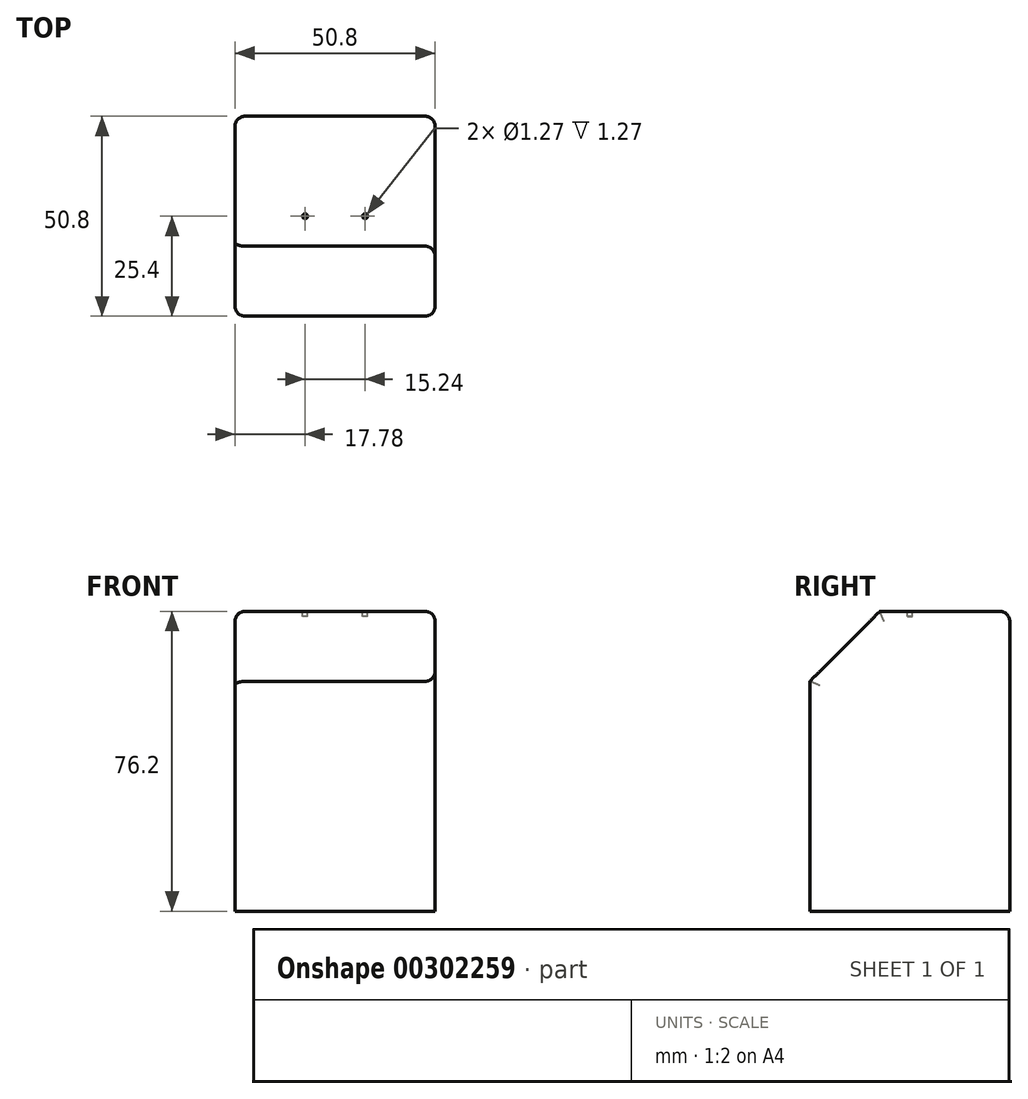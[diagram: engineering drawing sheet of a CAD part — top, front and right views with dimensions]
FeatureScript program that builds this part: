
annotation { "Feature Type Name" : "Feature", "Feature Type Description" : "" }
export const myFeature = defineFeature(function(context is Context, id is Id, definition is map)
    precondition{}
    {
        {
            var Q0;
            Q0=qCreatedBy(makeId("Top.planeOp"),FACE);
            var sketch = newSketch(context, id + "F0", { "sketchPlane" : qUnion([Q0])});
            skLineSegment(sketch, "E0.bottom", {"start": v(25.4, 25.4) * mm, "end": v(-25.4, 25.4) * mm});
            skLineSegment(sketch, "E0.top", {"start": v(25.4, -25.4) * mm, "end": v(-25.4, -25.4) * mm});
            skLineSegment(sketch, "E0.left", {"start": v(25.4, 25.4) * mm, "end": v(25.4, -25.4) * mm});
            skLineSegment(sketch, "E0.right", {"start": v(-25.4, 25.4) * mm, "end": v(-25.4, -25.4) * mm});
            skPoint(sketch, "E0.middle", {"position": v(0, 0) * mm});
            skSolve(sketch);
        }
        {
            var Q0;
            Q0 = qSketchRegion(id + "F0", true);
            extrude(context, id + "F1", {"entities" : qUnion([Q0]), "endBound" : BoundingType.SYMMETRIC, "depth" : 76.2 * mm});
        }
        {
            var Q0;
            Q0=makeQuery(id+"F1.opExtrude","CAP_FACE",FACE,{"disambiguationData":[OSD([sQuery(id+"F0.wireOp",EDGE,"E0.bottom"),sQuery(id+"F0.wireOp",EDGE,"E0.top"),sQuery(id+"F0.wireOp",EDGE,"E0.left"),sQuery(id+"F0.wireOp",EDGE,"E0.right")])],"isStart":false});
            var sketch = newSketch(context, id + "F2", { "sketchPlane" : qUnion([Q0])});
            skCircle(sketch, "E1", {"center": v(-7.62, 0) * mm, "radius": 0.64 * mm});
            skCircle(sketch, "E2", {"center": v(7.62, 0) * mm, "radius": 0.64 * mm});
            skSolve(sketch);
        }
        {
            var Q0;
            Q0 = qSketchRegion(id + "F2", true);
            extrude(context, id + "F3", {"entities" : qUnion([Q0]), "operationType" : NewBodyOperationType.REMOVE, "oppositeDirection" : true, "depth" : 1.27 * mm});
        }
        {
            var Q0;
            Q0=makeQuery(id+"F1.opExtrude","SWEPT_FACE",FACE,{"disambiguationData":[OSD([sQuery(id+"F0.wireOp",EDGE,"E0.left")])]});
            var sketch = newSketch(context, id + "F4", { "sketchPlane" : qUnion([Q0])});
            skLineSegment(sketch, "E3", {"start": v(-25.4, 20.32) * mm, "end": v(-7.62, 38.1) * mm});
            skLineSegment(sketch, "E4", {"start": v(-7.62, 38.1) * mm, "end": v(-25.4, 38.1) * mm});
            skLineSegment(sketch, "E5", {"start": v(-25.4, 38.1) * mm, "end": v(-25.4, 20.32) * mm});
            skSolve(sketch);
        }
        {
            var Q0;
            Q0 = qSketchRegion(id + "F4", true);
            extrude(context, id + "F5", {"entities" : qUnion([Q0]), "operationType" : NewBodyOperationType.REMOVE, "endBound" : BoundingType.THROUGH_ALL, "oppositeDirection" : true, "depth" : 25.4 * mm});
        }
        {
            var Q0;
            Q0=makeQuery(id+"F5.boolean.opBoolean","COPY",EDGE,{"derivedFrom":makeQuery(id+"F5.opExtrude","SWEPT_EDGE",EDGE,{"disambiguationData":[OSD([sQuery(id+"F0.wireOp",EDGE,"E0.left"),sQuery(id+"F4.wireOp",EDGE,"E3"),sQuery(id+"F4.wireOp",EDGE,"E4")])]})});
            var Q1;
            Q1=makeQuery(id+"F5.boolean.opBoolean","COPY",EDGE,{"derivedFrom":makeQuery(id+"F5.opExtrude","SWEPT_EDGE",EDGE,{"disambiguationData":[OSD([sQuery(id+"F0.wireOp",EDGE,"E0.top"),sQuery(id+"F0.wireOp",EDGE,"E0.left"),sQuery(id+"F4.wireOp",EDGE,"E3"),sQuery(id+"F4.wireOp",EDGE,"E5")])]})});
            var Q2;
            Q2=makeQuery(id+"F5.boolean.opBoolean","COPY",EDGE,{"derivedFrom":makeQuery(id+"F5.opExtrude","CAP_EDGE",EDGE,{"disambiguationData":[OSD([sQuery(id+"F4.wireOp",EDGE,"E3")])],"isStart":true})});
            var Q3;
            Q3=makeQuery(id+"F1.opExtrude","CAP_EDGE",EDGE,{"disambiguationData":[OSD([sQuery(id+"F0.wireOp",EDGE,"E0.left")])],"isStart":false});
            var Q4;
            Q4=makeQuery(id+"F1.opExtrude","CAP_EDGE",EDGE,{"disambiguationData":[OSD([sQuery(id+"F0.wireOp",EDGE,"E0.bottom")])],"isStart":false});
            var Q5;
            Q5=makeQuery(id+"F1.opExtrude","SWEPT_EDGE",EDGE,{"disambiguationData":[OSD([sQuery(id+"F0.wireOp",EDGE,"E0.bottom"),sQuery(id+"F0.wireOp",EDGE,"E0.left")])]});
            var Q6;
            Q6=makeQuery(id+"F1.opExtrude","CAP_EDGE",EDGE,{"disambiguationData":[OSD([sQuery(id+"F0.wireOp",EDGE,"E0.right")])],"isStart":false});
            var Q7;
            Q7=makeQuery(id+"F5.boolean.opBoolean","INTERSECT",EDGE,{"derivedFrom":[makeQuery(id+"F1.opExtrude","SWEPT_FACE",FACE,{"disambiguationData":[OSD([sQuery(id+"F0.wireOp",EDGE,"E0.right")])]}),makeQuery(id+"F5.opExtrude","SWEPT_FACE",FACE,{"disambiguationData":[OSD([sQuery(id+"F4.wireOp",EDGE,"E3")])]})]});
            var Q8;
            Q8=makeQuery(id+"F1.opExtrude","SWEPT_EDGE",EDGE,{"disambiguationData":[OSD([sQuery(id+"F0.wireOp",EDGE,"E0.top"),sQuery(id+"F0.wireOp",EDGE,"E0.left")])]});
            var Q9;
            Q9=makeQuery(id+"F1.opExtrude","SWEPT_EDGE",EDGE,{"disambiguationData":[OSD([sQuery(id+"F0.wireOp",EDGE,"E0.top"),sQuery(id+"F0.wireOp",EDGE,"E0.right")])]});
            var Q10;
            Q10=makeQuery(id+"F1.opExtrude","SWEPT_EDGE",EDGE,{"disambiguationData":[OSD([sQuery(id+"F0.wireOp",EDGE,"E0.bottom"),sQuery(id+"F0.wireOp",EDGE,"E0.right")])]});
            fillet(context, id + "F6", {"entities" : qUnion([Q0, Q1, Q2, Q3, Q4, Q5, Q6, Q7, Q8, Q9, Q10]), "radius" : 2.54 * mm, "tangentPropagation" : true, "allowEdgeOverflow" : false});
        }
    });
